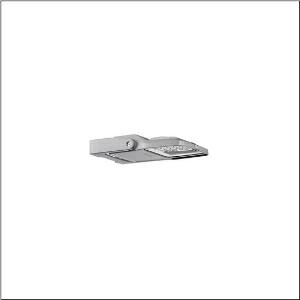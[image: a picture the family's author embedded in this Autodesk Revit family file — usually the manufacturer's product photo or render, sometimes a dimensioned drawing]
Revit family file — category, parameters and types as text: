
# Revit family: floodlight_fl_21_iq_micro___pl61_5xa7762a4c2a_69cd
name_source: partatom
category: Lighting Fixtures
units: mm (PartAtom-declared; Revit-internal decimal feet)

## family parameters
Cut with Voids When Loaded = No
Host = Face
Light Source = No
Part Type = Normal
Room Calculation Point = No
Round Connector Dimension = Use Diameter
Shared = No

## types (1)
- --- (1 x LED, 3030 lm, 23.1 W, 4000K)
    Apparent Load = 23 VA
    CIE Flux Codes = 33 65 98 100 100
    Color Rendering = 70
    Color Temperature = 4000K
    Default Elevation = 1800 mm
    Description = Floodlight FL 21 iQ micro, floodlight, primary light control with lens, of PMMA, primary optical cover: protective disc, of toughened safety glass, transparent, light distribution: PL61, light emission: direct distribution, installation type: surface-mounted, LED, High Power LED, rated luminous flux: 3.030lm, luminous efficacy: 131lm/W, light colour: 740, colour temperature: 4000K, control: Auto-Match, Temp-Guard, Night-Set, Smart-Wire, Desk-Remote (wireless, voltage-free reading and setting of iQ features in the workshop via application-optimized NFC function/RFID function), optimised constant luminous flux control (CLO 2.0), Street-Remote, with terminal, 6-pole, mains connection: 220..240V, AC, 50/60Hz, start of lifetime: 23W, end of service life: 24W, reduction: 11W, luminaire housing, of diecast aluminium, powder-coated, Siteco® metallic grey (DB 702S), corrosivity category C5 mid according to DIN EN ISO 12944, sealing non-destructively replaceable, design bracket, of diecast aluminium, powder-coated, Siteco® metallic grey (DB 702S), protection rating (complete): IP66, insulation class (complete): insulation class II (safety insulation), certification: CE, ENEC, VDE, protection symbol: D, impact resistance: IK07, permissible operating ambient temperature: -40..+40°C, permissible operating ambient temperature for outdoor applications: -40..+50°C, standard: DIN EN 12944, LABS conformity tested according to VDMA 24364:2018-05, packaging unit: 1 piece

Light Distribution: PL61
    Height = 65 mm
    Lamp = 1 x LED
    Lamp Light Flux = 3030 lm
    Lamp Power = 23.1 W
    Lamp count = 1
    Length = 312 mm
    Luminous efficacy = 131 lm/W
    Manufacturer = Siteco
    ModVariant = No
    Model = 5XA7762A4C2A
    Mounting Place = Wall
    Mounting Type = Surface mounted
    Number of Poles = 1
    OnlyDefault = Yes
    Power Factor = 1
    Product Name = Floodlight FL 21 iQ micro | PL61
    Product group = floodlight | wall mounted
    ProductGroupID = 2001
    Protection Class = Protection class II
    Protection Degree = IP 66
    RLX_Detail_Level = 1
    RLX_Emergency_Light_Flux = 0 lm
    RLX_Emergency_Type = 0
    RLX_Emergency_Type_DB = No
    RlxData = <blob elided: 97425 chars, md5=4b4c0c9d>
    Socket = socket
    Standby Power = 0 W
    System Light Flux = 3030 lm
    System Power = 23 W
    Type Comments = factory setting: luminous flux: 100 % | dim-lin: 254 | 455 mA
    Type Image = l_1006878.jpg
    URL = http://relux.com
    VarID = @adj_166981
    Voltage = 0 V
    Weight = 0.00 kg
    Width = 230 mm

## geometry (parser evidence)
native form markers: Blend x4, Sweep x14
no freeform markers — native parametric forms only
